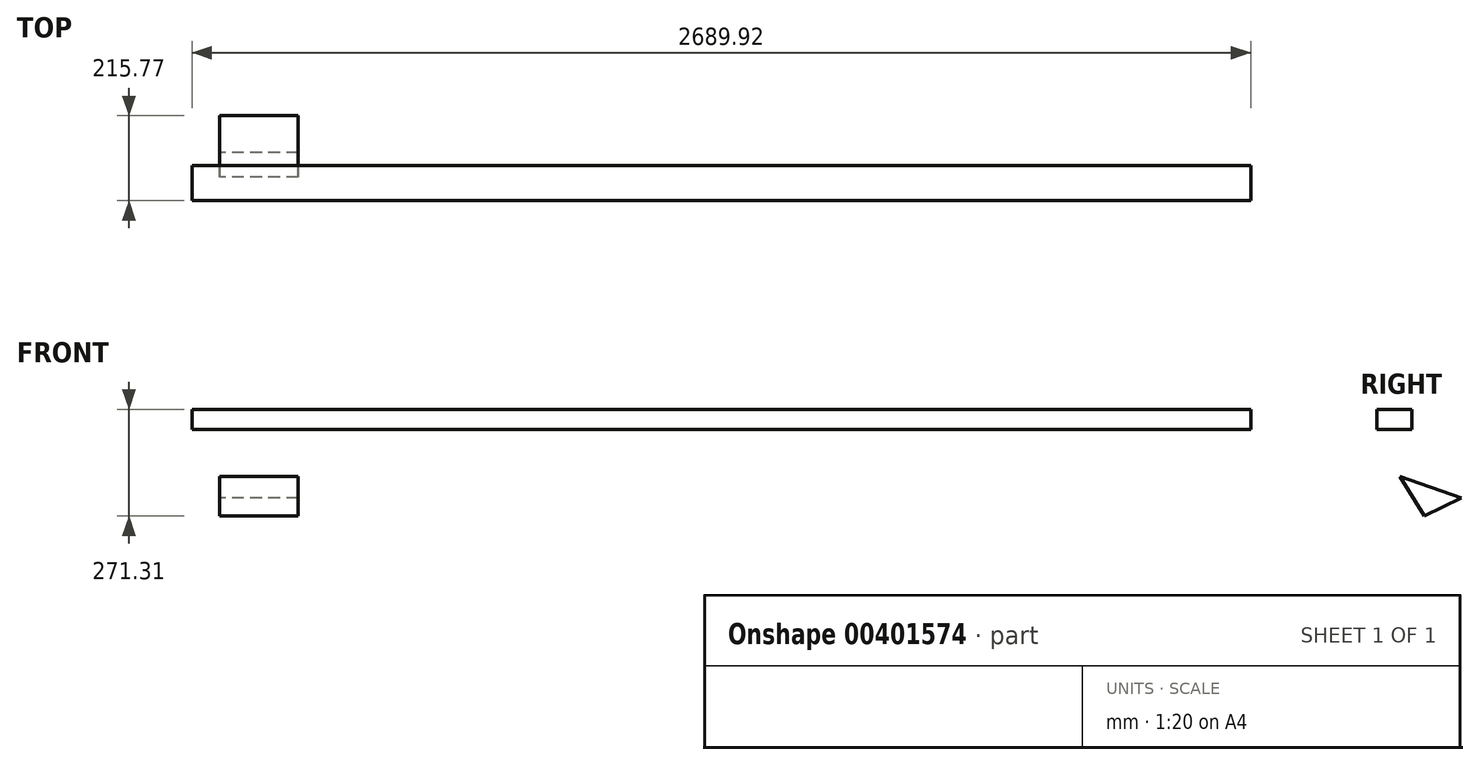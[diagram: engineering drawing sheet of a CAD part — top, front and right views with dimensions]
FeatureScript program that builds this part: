
annotation { "Feature Type Name" : "Feature", "Feature Type Description" : "" }
export const myFeature = defineFeature(function(context is Context, id is Id, definition is map)
    precondition{}
    {
        {
            var Q0;
            Q0=qCreatedBy(makeId("Front.planeOp"),FACE);
            var sketch = newSketch(context, id + "F0", { "sketchPlane" : qUnion([Q0])});
            skLineSegment(sketch, "E0.bottom", {"start": v(-71.06, 24.79) * mm, "end": v(180.46, 24.79) * mm});
            skLineSegment(sketch, "E0.top", {"start": v(-71.06, 11.38) * mm, "end": v(180.46, 11.38) * mm});
            skLineSegment(sketch, "E0.left", {"start": v(-71.06, 24.79) * mm, "end": v(-71.06, 11.38) * mm});
            skLineSegment(sketch, "E0.right", {"start": v(180.46, 24.79) * mm, "end": v(180.46, 11.38) * mm});
            skSolve(sketch);
        }
        {
            var Q0;
            Q0 = qSketchRegion(id + "F0", true);
            var sketch = newSketch(context, id + "F1", { "sketchPlane" : qUnion([Q0])});
            skSolve(sketch);
        }
        {
            var Q0;
            Q0=makeQuery(id+"F1.imprint","IMPRINT",FACE,{"disambiguationData":[TD([[makeQuery(id+"F1.imprint","IMPRINT",EDGE,{"derivedFrom":makeQuery(id+"F0.imprint","IMPRINT",EDGE,{"derivedFrom":sQuery(id+"F0.wireOp",EDGE,"E0.bottom")})}),-1.0]])]});
            extrude(context, id + "F2", {"entities" : qUnion([Q0]), "depth" : 88.9 * mm});
        }
        {
            var Q0;
            Q0=makeQuery(id+"F2.opExtrude","SWEPT_FACE",FACE,{"disambiguationData":[OSD([sQuery(id+"F0.wireOp",EDGE,"E0.bottom")])]});
            extrude(context, id + "F3", {"entities" : qUnion([Q0]), "operationType" : NewBodyOperationType.ADD, "depth" : 38.1 * mm});
        }
        {
            var Q0;
            {var subQ0=sQuery(id+"F0.wireOp",EDGE,"E0.right");Q0=makeQuery(id+"F3.boolean.opBoolean","MERGE",FACE,{"derivedFrom":[makeQuery(id+"F2.opExtrude","SWEPT_FACE",FACE,{"disambiguationData":[OSD([subQ0])]}),makeQuery(id+"F3.opExtrude","SWEPT_FACE",FACE,{"disambiguationData":[OSD([sQuery(id+"F0.wireOp",EDGE,"E0.bottom"),subQ0])]})]});}
            extrude(context, id + "F4", {"entities" : qUnion([Q0]), "operationType" : NewBodyOperationType.ADD, "depth" : 2438.4 * mm});
        }
        {
            var Q0;
            Q0=qCreatedBy(makeId("Right.planeOp"), FACE);
            var sketch = newSketch(context, id + "F5", { "sketchPlane" : qUnion([Q0])});
            skLineSegment(sketch, "E1", {"start": v(126.87, -161.83) * mm, "end": v(-29.3, -107.75) * mm});
            skLineSegment(sketch, "E2", {"start": v(-29.3, -107.75) * mm, "end": v(32.96, -208.42) * mm});
            skLineSegment(sketch, "E3", {"start": v(32.96, -208.42) * mm, "end": v(126.87, -161.83) * mm});
            skSolve(sketch);
        }
        {
            var Q0;
            Q0 = qSketchRegion(id + "F5", true);
            extrude(context, id + "F6", {"entities" : qUnion([Q0]), "domain" : OperationDomain.MODEL, "flatOperationType" : FlatOperationType.REMOVE, "depth" : 199.03 * mm, "offsetDistance" : 25.4 * mm});
        }
    });
